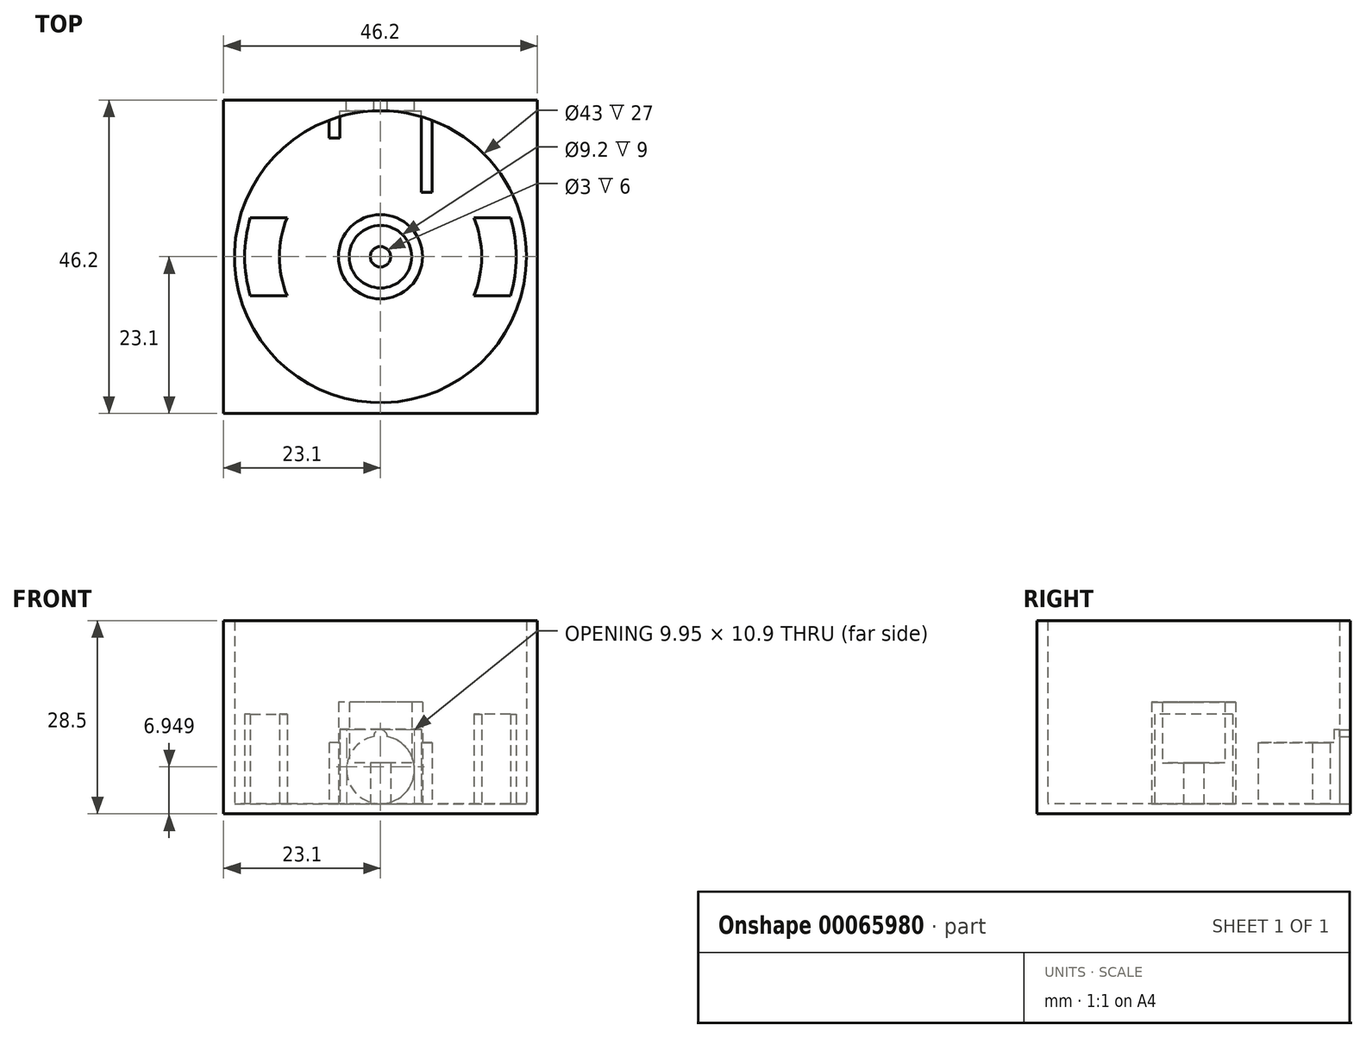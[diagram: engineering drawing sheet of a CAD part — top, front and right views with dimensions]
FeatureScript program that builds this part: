
annotation { "Feature Type Name" : "Feature", "Feature Type Description" : "" }
export const myFeature = defineFeature(function(context is Context, id is Id, definition is map)
    precondition{}
    {
        {
            var Q0;
            Q0=qCreatedBy(makeId("Top.planeOp"),FACE);
            var sketch = newSketch(context, id + "F0", { "sketchPlane" : qUnion([Q0])});
            skLineSegment(sketch, "E0.bottom", {"start": v(0, 0) * mm, "end": v(46.2, 0) * mm});
            skLineSegment(sketch, "E0.top", {"start": v(0, 46.2) * mm, "end": v(46.2, 46.2) * mm});
            skLineSegment(sketch, "E0.left", {"start": v(0, 0) * mm, "end": v(0, 46.2) * mm});
            skLineSegment(sketch, "E0.right", {"start": v(46.2, 0) * mm, "end": v(46.2, 46.2) * mm});
            skSolve(sketch);
        }
        {
            var Q0;
            Q0=makeQuery(id+"F0.imprint","IMPRINT",FACE,{"disambiguationData":[TD([[makeQuery(id+"F0.imprint","IMPRINT",EDGE,{"derivedFrom":sQuery(id+"F0.wireOp",EDGE,"E0.bottom")}),1.0]])]});
            extrude(context, id + "F1", {"entities" : qUnion([Q0]), "depth" : 1.5 * mm});
        }
        {
            var Q0;
            Q0=makeQuery(id+"F1.opExtrude","CAP_FACE",FACE,{"disambiguationData":[OSD([sQuery(id+"F0.wireOp",EDGE,"E0.bottom"),sQuery(id+"F0.wireOp",EDGE,"E0.top"),sQuery(id+"F0.wireOp",EDGE,"E0.left"),sQuery(id+"F0.wireOp",EDGE,"E0.right")])],"isStart":false});
            var sketch = newSketch(context, id + "F2", { "sketchPlane" : qUnion([Q0])});
            skLineSegment(sketch, "E1.bottom", {"start": v(0, 0) * mm, "end": v(46.2, 0) * mm});
            skLineSegment(sketch, "E1.top", {"start": v(0, 46.2) * mm, "end": v(46.2, 46.2) * mm});
            skLineSegment(sketch, "E1.left", {"start": v(0, 0) * mm, "end": v(0, 46.2) * mm});
            skLineSegment(sketch, "E1.right", {"start": v(46.2, 0) * mm, "end": v(46.2, 46.2) * mm});
            skCircle(sketch, "E2", {"center": v(23.1, 23.1) * mm, "radius": 21.5 * mm});
            skSolve(sketch);
        }
        {
            var Q0;
            Q0 = qSketchRegion(id + "F2", true);
            extrude(context, id + "F3", {"entities" : qUnion([Q0]), "operationType" : NewBodyOperationType.ADD, "depth" : 27 * mm});
        }
        {
            var Q0;
            Q0=makeQuery(id+"F1.opExtrude","CAP_FACE",FACE,{"disambiguationData":[OSD([sQuery(id+"F0.wireOp",EDGE,"E0.bottom"),sQuery(id+"F0.wireOp",EDGE,"E0.top"),sQuery(id+"F0.wireOp",EDGE,"E0.left"),sQuery(id+"F0.wireOp",EDGE,"E0.right")])],"isStart":false});
            var sketch = newSketch(context, id + "F4", { "sketchPlane" : qUnion([Q0])});
            skCircle(sketch, "E3", {"center": v(23.1, 23.1) * mm, "radius": 6.2 * mm});
            skCircle(sketch, "E4", {"center": v(23.1, 23.1) * mm, "radius": 1.5 * mm});
            skSolve(sketch);
        }
        {
            var Q0;
            Q0 = qSketchRegion(id + "F4", true);
            extrude(context, id + "F5", {"entities" : qUnion([Q0]), "operationType" : NewBodyOperationType.ADD, "depth" : 6 * mm});
        }
        {
            var Q0;
            Q0=makeQuery(id+"F5.opExtrude","CAP_FACE",FACE,{"disambiguationData":[OSD([sQuery(id+"F4.wireOp",EDGE,"E3"),sQuery(id+"F4.wireOp",EDGE,"E4")])],"isStart":false});
            var sketch = newSketch(context, id + "F6", { "sketchPlane" : qUnion([Q0])});
            skCircle(sketch, "E5", {"center": v(23.1, 23.1) * mm, "radius": 6.2 * mm});
            skCircle(sketch, "E6", {"center": v(23.1, 23.1) * mm, "radius": 4.6 * mm});
            skSolve(sketch);
        }
        {
            var Q0;
            Q0 = qSketchRegion(id + "F6", true);
            extrude(context, id + "F7", {"entities" : qUnion([Q0]), "operationType" : NewBodyOperationType.ADD, "depth" : 9 * mm});
        }
        {
            var Q0;
            Q0=makeQuery(id+"F5.boolean.opBoolean","SPLIT",FACE,{"disambiguationData":[TD([makeQuery(id+"F3.opExtrude","SWEPT_FACE",FACE,{"disambiguationData":[OSD([sQuery(id+"F2.wireOp",EDGE,"E2")])]})])],"derivedFrom":makeQuery(id+"F1.opExtrude","CAP_FACE",FACE,{"disambiguationData":[OSD([sQuery(id+"F0.wireOp",EDGE,"E0.bottom"),sQuery(id+"F0.wireOp",EDGE,"E0.top"),sQuery(id+"F0.wireOp",EDGE,"E0.left"),sQuery(id+"F0.wireOp",EDGE,"E0.right")])],"isStart":false})});
            var sketch = newSketch(context, id + "F8", { "sketchPlane" : qUnion([Q0])});
            skArc(sketch, "E7", {"start": v(3.94, 17.38) * mm, "mid": v(3.1, 23.1) * mm, "end": v(3.94, 28.82) * mm});
            skArc(sketch, "E8", {"start": v(9.34, 17.38) * mm, "mid": v(8.2, 23.1) * mm, "end": v(9.34, 28.82) * mm});
            skLineSegment(sketch, "E9", {"start": v(3.94, 28.82) * mm, "end": v(9.34, 28.82) * mm});
            skLineSegment(sketch, "E10", {"start": v(3.94, 17.38) * mm, "end": v(9.34, 17.38) * mm});
            skLineSegment(sketch, "E11", {"start": v(23.1, 46.21) * mm, "end": v(23.1, 0) * mm, "construction": true});
            skLineSegment(sketch, "E12.MirrorCS", {"start": v(42.26, 28.82) * mm, "end": v(36.86, 28.82) * mm});
            skArc(sketch, "E13.MirrorCS", {"start": v(42.26, 17.38) * mm, "mid": v(43.1, 23.1) * mm, "end": v(42.26, 28.82) * mm});
            skArc(sketch, "E14.MirrorCS", {"start": v(36.86, 17.38) * mm, "mid": v(38, 23.1) * mm, "end": v(36.86, 28.82) * mm});
            skLineSegment(sketch, "E15.MirrorCS", {"start": v(42.26, 17.38) * mm, "end": v(36.86, 17.38) * mm});
            skSolve(sketch);
        }
        {
            var Q0;
            Q0 = qSketchRegion(id + "F8", true);
            extrude(context, id + "F9", {"entities" : qUnion([Q0]), "operationType" : NewBodyOperationType.ADD, "depth" : 13.2 * mm});
        }
        {
            var Q0;
            Q0=makeQuery(id+"F3.boolean.opBoolean","MERGE",FACE,{"derivedFrom":[makeQuery(id+"F1.opExtrude","SWEPT_FACE",FACE,{"disambiguationData":[OSD([sQuery(id+"F0.wireOp",EDGE,"E0.top")])]}),makeQuery(id+"F3.opExtrude","SWEPT_FACE",FACE,{"disambiguationData":[OSD([sQuery(id+"F2.wireOp",EDGE,"E1.top")])]})]});
            var sketch = newSketch(context, id + "F10", { "sketchPlane" : qUnion([Q0])});
            skArc(sketch, "E16", {"start": v(-22.1, 11.4) * mm, "mid": v(-23.1, 1.5) * mm, "end": v(-24.1, 11.4) * mm});
            skArc(sketch, "E17", {"start": v(-24.1, 11.4) * mm, "mid": v(-23.1, 12.4) * mm, "end": v(-22.1, 11.4) * mm});
            skSolve(sketch);
        }
        {
            var Q0;
            Q0 = qSketchRegion(id + "F10", true);
            var Q1;
            Q1=makeQuery(id+"F3.opExtrude","SWEPT_FACE",FACE,{"disambiguationData":[OSD([sQuery(id+"F2.wireOp",EDGE,"E2")])]});
            extrude(context, id + "F11", {"entities" : qUnion([Q0]), "operationType" : NewBodyOperationType.REMOVE, "endBound" : BoundingType.UP_TO_SURFACE, "oppositeDirection" : true, "endBoundEntityFace" : qUnion([Q1]), "depth" : 25 * mm});
        }
        {
            var Q0;
            Q0=makeQuery(id+"F5.boolean.opBoolean","SPLIT",FACE,{"disambiguationData":[TD([makeQuery(id+"F3.opExtrude","SWEPT_FACE",FACE,{"disambiguationData":[OSD([sQuery(id+"F2.wireOp",EDGE,"E2")])]})])],"derivedFrom":makeQuery(id+"F1.opExtrude","CAP_FACE",FACE,{"disambiguationData":[OSD([sQuery(id+"F0.wireOp",EDGE,"E0.bottom"),sQuery(id+"F0.wireOp",EDGE,"E0.top"),sQuery(id+"F0.wireOp",EDGE,"E0.left"),sQuery(id+"F0.wireOp",EDGE,"E0.right")])],"isStart":false})});
            var sketch = newSketch(context, id + "F12", { "sketchPlane" : qUnion([Q0])});
            skLineSegment(sketch, "E18.bottom", {"start": v(17.1, 29.6) * mm, "end": v(29.1, 29.6) * mm});
            skLineSegment(sketch, "E18.top", {"start": v(17.1, 44.6) * mm, "end": v(29.1, 44.6) * mm});
            skLineSegment(sketch, "E18.left", {"start": v(17.1, 29.6) * mm, "end": v(17.1, 44.6) * mm});
            skLineSegment(sketch, "E18.right", {"start": v(29.1, 29.6) * mm, "end": v(29.1, 44.6) * mm});
            skSolve(sketch);
        }
        {
            var Q0;
            Q0 = qSketchRegion(id + "F12", true);
            extrude(context, id + "F13", {"entities" : qUnion([Q0]), "operationType" : NewBodyOperationType.REMOVE, "depth" : 11 * mm});
        }
        {
            var Q0;
            Q0=makeQuery(id+"F13.boolean.opBoolean","MERGE",FACE,{"derivedFrom":[makeQuery(id+"F5.boolean.opBoolean","SPLIT",FACE,{"disambiguationData":[TD([makeQuery(id+"F3.opExtrude","SWEPT_FACE",FACE,{"disambiguationData":[OSD([sQuery(id+"F2.wireOp",EDGE,"E2")])]})])],"derivedFrom":makeQuery(id+"F1.opExtrude","CAP_FACE",FACE,{"disambiguationData":[OSD([sQuery(id+"F0.wireOp",EDGE,"E0.bottom"),sQuery(id+"F0.wireOp",EDGE,"E0.top"),sQuery(id+"F0.wireOp",EDGE,"E0.left"),sQuery(id+"F0.wireOp",EDGE,"E0.right")])],"isStart":false})}),makeQuery(id+"F13.opExtrude","CAP_FACE",FACE,{"disambiguationData":[OSD([sQuery(id+"F12.wireOp",EDGE,"E18.bottom"),sQuery(id+"F12.wireOp",EDGE,"E18.top"),sQuery(id+"F12.wireOp",EDGE,"E18.left"),sQuery(id+"F12.wireOp",EDGE,"E18.right")])],"isStart":true})]});
            var sketch = newSketch(context, id + "F14", { "sketchPlane" : qUnion([Q0])});
            skLineSegment(sketch, "E19", {"start": v(17.1, 43.75) * mm, "end": v(17.1, 40.6) * mm});
            skLineSegment(sketch, "E20", {"start": v(17.1, 40.6) * mm, "end": v(15.5, 40.6) * mm});
            skLineSegment(sketch, "E21", {"start": v(15.5, 40.6) * mm, "end": v(15.5, 43.21) * mm});
            skLineSegment(sketch, "E22", {"start": v(29.1, 43.75) * mm, "end": v(29.1, 32.6) * mm});
            skLineSegment(sketch, "E23", {"start": v(29.1, 32.6) * mm, "end": v(30.7, 32.6) * mm});
            skLineSegment(sketch, "E24", {"start": v(30.7, 32.6) * mm, "end": v(30.7, 43.21) * mm});
            skArc(sketch, "E25", {"start": v(15.5, 43.21) * mm, "mid": v(16.3, 43.5) * mm, "end": v(17.1, 43.75) * mm});
            skArc(sketch, "E26", {"start": v(29.1, 43.75) * mm, "mid": v(29.9, 43.5) * mm, "end": v(30.7, 43.21) * mm});
            skSolve(sketch);
        }
        {
            var Q0;
            Q0 = qSketchRegion(id + "F14", true);
            extrude(context, id + "F15", {"entities" : qUnion([Q0]), "operationType" : NewBodyOperationType.ADD, "depth" : 9 * mm});
        }
    });
